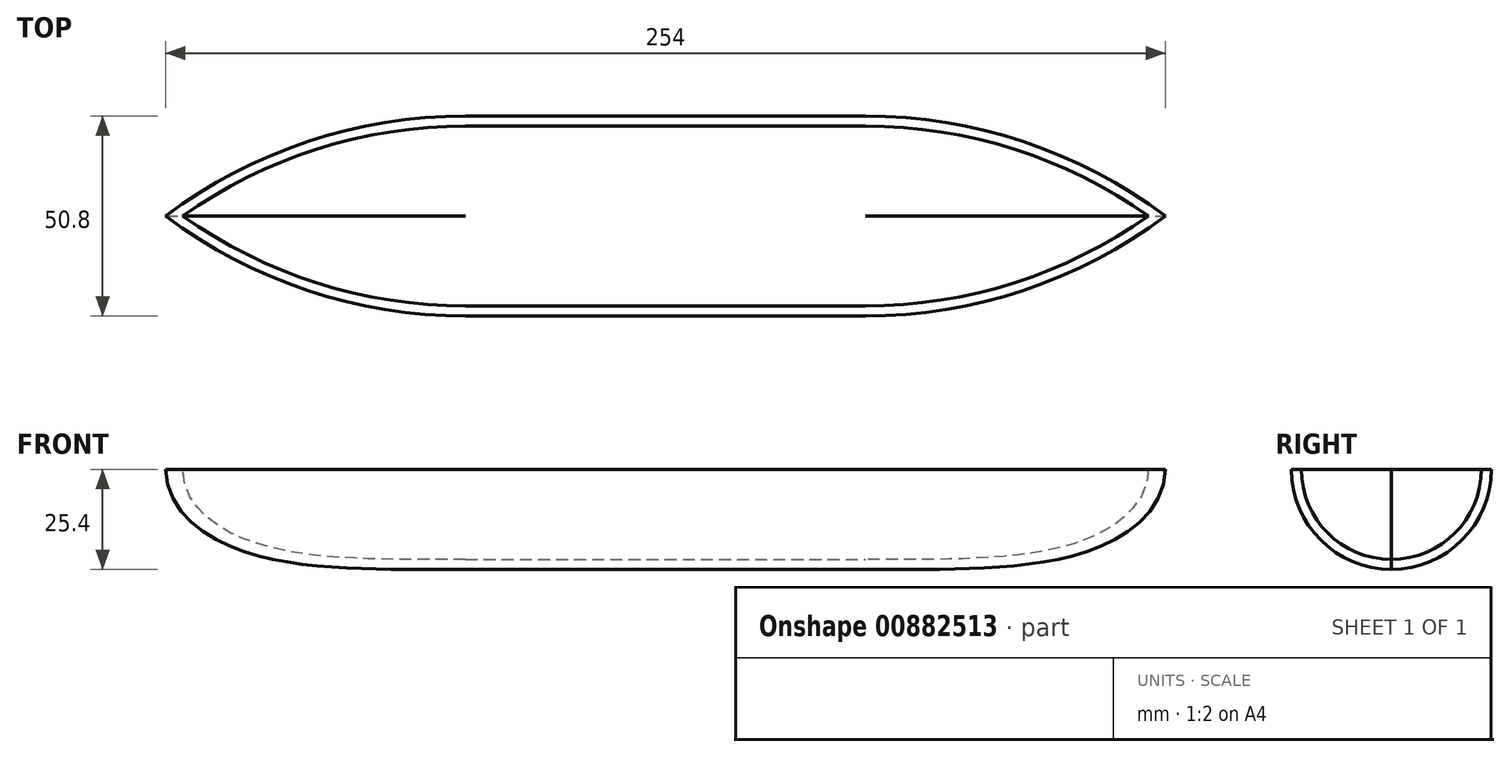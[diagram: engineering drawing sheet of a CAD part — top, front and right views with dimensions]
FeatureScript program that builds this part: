
annotation { "Feature Type Name" : "Feature", "Feature Type Description" : "" }
export const myFeature = defineFeature(function(context is Context, id is Id, definition is map)
    precondition{}
    {
        {
            var Q0;
            Q0=qCreatedBy(makeId("Top.planeOp"),FACE);
            var sketch = newSketch(context, id + "F0", { "sketchPlane" : qUnion([Q0])});
            skLineSegment(sketch, "E0.bottom", {"start": v(-127, 25.4) * mm, "end": v(127, 25.4) * mm});
            skLineSegment(sketch, "E0.top", {"start": v(-127, -25.4) * mm, "end": v(127, -25.4) * mm});
            skLineSegment(sketch, "E0.left", {"start": v(-127, 25.4) * mm, "end": v(-127, -25.4) * mm});
            skLineSegment(sketch, "E0.right", {"start": v(127, 25.4) * mm, "end": v(127, -25.4) * mm});
            skPoint(sketch, "E0.middle", {"position": v(0, 0) * mm});
            skSolve(sketch);
        }
        {
            var Q0;
            Q0=makeQuery(id+"F0.imprint","IMPRINT",FACE,{"disambiguationData":[TD([[makeQuery(id+"F0.imprint","IMPRINT",EDGE,{"derivedFrom":sQuery(id+"F0.wireOp",EDGE,"E0.bottom")}),-1.0]])]});
            extrude(context, id + "F1", {"entities" : qUnion([Q0]), "depth" : 25.4 * mm, "offsetDistance" : 25.4 * mm});
        }
        {
            var Q0;
            Q0=makeQuery(id+"F1.opExtrude","SWEPT_EDGE",EDGE,{"disambiguationData":[OSD([sQuery(id+"F0.wireOp",EDGE,"E0.top"),sQuery(id+"F0.wireOp",EDGE,"E0.right")])]});
            var Q1;
            Q1=makeQuery(id+"F1.opExtrude","SWEPT_EDGE",EDGE,{"disambiguationData":[OSD([sQuery(id+"F0.wireOp",EDGE,"E0.bottom"),sQuery(id+"F0.wireOp",EDGE,"E0.right")])]});
            var Q2;
            Q2=makeQuery(id+"F1.opExtrude","SWEPT_EDGE",EDGE,{"disambiguationData":[OSD([sQuery(id+"F0.wireOp",EDGE,"E0.top"),sQuery(id+"F0.wireOp",EDGE,"E0.left")])]});
            var Q3;
            Q3=makeQuery(id+"F1.opExtrude","SWEPT_EDGE",EDGE,{"disambiguationData":[OSD([sQuery(id+"F0.wireOp",EDGE,"E0.bottom"),sQuery(id+"F0.wireOp",EDGE,"E0.left")])]});
            chamfer(context, id + "F2", {"entities" : qUnion([Q0, Q1, Q2, Q3]), "width" : 25.4 * mm, "tangentPropagation" : true});
        }
        {
            var Q0;
            {var subQ0=sQuery(id+"F0.wireOp",EDGE,"E0.top");Q0=makeQuery(id+"F2.opChamfer","BLEND_EDGE",EDGE,{"blendedFrom":[makeQuery(id+"F1.opExtrude","SWEPT_EDGE",EDGE,{"disambiguationData":[OSD([subQ0,sQuery(id+"F0.wireOp",EDGE,"E0.right")])]}),makeQuery(id+"F1.opExtrude","SWEPT_FACE",FACE,{"disambiguationData":[OSD([subQ0])]})],"blendedInto":[makeQuery(id+"F1.opExtrude","SWEPT_FACE",FACE,{"disambiguationData":[OSD([subQ0])]})]});}
            var Q1;
            {var subQ0=sQuery(id+"F0.wireOp",EDGE,"E0.top");Q1=makeQuery(id+"F2.opChamfer","BLEND_EDGE",EDGE,{"blendedFrom":[makeQuery(id+"F1.opExtrude","SWEPT_EDGE",EDGE,{"disambiguationData":[OSD([subQ0,sQuery(id+"F0.wireOp",EDGE,"E0.left")])]}),makeQuery(id+"F1.opExtrude","SWEPT_FACE",FACE,{"disambiguationData":[OSD([subQ0])]})],"blendedInto":[makeQuery(id+"F1.opExtrude","SWEPT_FACE",FACE,{"disambiguationData":[OSD([subQ0])]})]});}
            var Q2;
            {var subQ0=sQuery(id+"F0.wireOp",EDGE,"E0.bottom");Q2=makeQuery(id+"F2.opChamfer","BLEND_EDGE",EDGE,{"blendedFrom":[makeQuery(id+"F1.opExtrude","SWEPT_EDGE",EDGE,{"disambiguationData":[OSD([subQ0,sQuery(id+"F0.wireOp",EDGE,"E0.right")])]}),makeQuery(id+"F1.opExtrude","SWEPT_FACE",FACE,{"disambiguationData":[OSD([subQ0])]})],"blendedInto":[makeQuery(id+"F1.opExtrude","SWEPT_FACE",FACE,{"disambiguationData":[OSD([subQ0])]})]});}
            var Q3;
            {var subQ0=sQuery(id+"F0.wireOp",EDGE,"E0.bottom");Q3=makeQuery(id+"F2.opChamfer","BLEND_EDGE",EDGE,{"blendedFrom":[makeQuery(id+"F1.opExtrude","SWEPT_EDGE",EDGE,{"disambiguationData":[OSD([subQ0,sQuery(id+"F0.wireOp",EDGE,"E0.left")])]}),makeQuery(id+"F1.opExtrude","SWEPT_FACE",FACE,{"disambiguationData":[OSD([subQ0])]})],"blendedInto":[makeQuery(id+"F1.opExtrude","SWEPT_FACE",FACE,{"disambiguationData":[OSD([subQ0])]})]});}
            fillet(context, id + "F3", {"entities" : qUnion([Q0, Q1, Q2, Q3]), "radius" : 127 * mm, "tangentPropagation" : true, "allowEdgeOverflow" : false});
        }
        {
            var Q0;
            {var subQ0=sQuery(id+"F0.wireOp",EDGE,"E0.left");var subQ1=sQuery(id+"F0.wireOp",EDGE,"E0.top");Q0=makeQuery(id+"F3.opFillet","BLEND_EDGE",EDGE,{"blendedFrom":[makeQuery(id+"F2.opChamfer","BLEND_EDGE",EDGE,{"blendedFrom":[makeQuery(id+"F1.opExtrude","SWEPT_EDGE",EDGE,{"disambiguationData":[OSD([subQ1,subQ0])]}),makeQuery(id+"F1.opExtrude","SWEPT_FACE",FACE,{"disambiguationData":[OSD([subQ1])]})],"blendedInto":[makeQuery(id+"F1.opExtrude","SWEPT_FACE",FACE,{"disambiguationData":[OSD([subQ1])]})]}),makeQuery(id+"F1.opExtrude","CAP_FACE",FACE,{"disambiguationData":[OSD([sQuery(id+"F0.wireOp",EDGE,"E0.bottom"),subQ1,subQ0,sQuery(id+"F0.wireOp",EDGE,"E0.right")])],"isStart":true})],"blendedInto":[makeQuery(id+"F1.opExtrude","CAP_FACE",FACE,{"disambiguationData":[OSD([sQuery(id+"F0.wireOp",EDGE,"E0.bottom"),subQ1,subQ0,sQuery(id+"F0.wireOp",EDGE,"E0.right")])],"isStart":true})]});}
            var Q1;
            Q1=makeQuery(id+"F1.opExtrude","CAP_EDGE",EDGE,{"disambiguationData":[OSD([sQuery(id+"F0.wireOp",EDGE,"E0.top")])],"isStart":true});
            var Q2;
            {var subQ0=sQuery(id+"F0.wireOp",EDGE,"E0.right");var subQ1=sQuery(id+"F0.wireOp",EDGE,"E0.top");Q2=makeQuery(id+"F3.opFillet","BLEND_EDGE",EDGE,{"blendedFrom":[makeQuery(id+"F2.opChamfer","BLEND_EDGE",EDGE,{"blendedFrom":[makeQuery(id+"F1.opExtrude","SWEPT_EDGE",EDGE,{"disambiguationData":[OSD([subQ1,subQ0])]}),makeQuery(id+"F1.opExtrude","SWEPT_FACE",FACE,{"disambiguationData":[OSD([subQ1])]})],"blendedInto":[makeQuery(id+"F1.opExtrude","SWEPT_FACE",FACE,{"disambiguationData":[OSD([subQ1])]})]}),makeQuery(id+"F1.opExtrude","CAP_FACE",FACE,{"disambiguationData":[OSD([sQuery(id+"F0.wireOp",EDGE,"E0.bottom"),subQ1,sQuery(id+"F0.wireOp",EDGE,"E0.left"),subQ0])],"isStart":true})],"blendedInto":[makeQuery(id+"F1.opExtrude","CAP_FACE",FACE,{"disambiguationData":[OSD([sQuery(id+"F0.wireOp",EDGE,"E0.bottom"),subQ1,sQuery(id+"F0.wireOp",EDGE,"E0.left"),subQ0])],"isStart":true})]});}
            var Q3;
            {var subQ0=sQuery(id+"F0.wireOp",EDGE,"E0.right");var subQ1=sQuery(id+"F0.wireOp",EDGE,"E0.bottom");Q3=makeQuery(id+"F3.opFillet","BLEND_EDGE",EDGE,{"blendedFrom":[makeQuery(id+"F2.opChamfer","BLEND_EDGE",EDGE,{"blendedFrom":[makeQuery(id+"F1.opExtrude","SWEPT_EDGE",EDGE,{"disambiguationData":[OSD([subQ1,subQ0])]}),makeQuery(id+"F1.opExtrude","SWEPT_FACE",FACE,{"disambiguationData":[OSD([subQ1])]})],"blendedInto":[makeQuery(id+"F1.opExtrude","SWEPT_FACE",FACE,{"disambiguationData":[OSD([subQ1])]})]}),makeQuery(id+"F1.opExtrude","CAP_FACE",FACE,{"disambiguationData":[OSD([subQ1,sQuery(id+"F0.wireOp",EDGE,"E0.top"),sQuery(id+"F0.wireOp",EDGE,"E0.left"),subQ0])],"isStart":true})],"blendedInto":[makeQuery(id+"F1.opExtrude","CAP_FACE",FACE,{"disambiguationData":[OSD([subQ1,sQuery(id+"F0.wireOp",EDGE,"E0.top"),sQuery(id+"F0.wireOp",EDGE,"E0.left"),subQ0])],"isStart":true})]});}
            var Q4;
            Q4=makeQuery(id+"F1.opExtrude","CAP_EDGE",EDGE,{"disambiguationData":[OSD([sQuery(id+"F0.wireOp",EDGE,"E0.bottom")])],"isStart":true});
            var Q5;
            {var subQ0=sQuery(id+"F0.wireOp",EDGE,"E0.left");var subQ1=sQuery(id+"F0.wireOp",EDGE,"E0.bottom");Q5=makeQuery(id+"F3.opFillet","BLEND_EDGE",EDGE,{"blendedFrom":[makeQuery(id+"F2.opChamfer","BLEND_EDGE",EDGE,{"blendedFrom":[makeQuery(id+"F1.opExtrude","SWEPT_EDGE",EDGE,{"disambiguationData":[OSD([subQ1,subQ0])]}),makeQuery(id+"F1.opExtrude","SWEPT_FACE",FACE,{"disambiguationData":[OSD([subQ1])]})],"blendedInto":[makeQuery(id+"F1.opExtrude","SWEPT_FACE",FACE,{"disambiguationData":[OSD([subQ1])]})]}),makeQuery(id+"F1.opExtrude","CAP_FACE",FACE,{"disambiguationData":[OSD([subQ1,sQuery(id+"F0.wireOp",EDGE,"E0.top"),subQ0,sQuery(id+"F0.wireOp",EDGE,"E0.right")])],"isStart":true})],"blendedInto":[makeQuery(id+"F1.opExtrude","CAP_FACE",FACE,{"disambiguationData":[OSD([subQ1,sQuery(id+"F0.wireOp",EDGE,"E0.top"),subQ0,sQuery(id+"F0.wireOp",EDGE,"E0.right")])],"isStart":true})]});}
            fillet(context, id + "F4", {"entities" : qUnion([Q0, Q1, Q2, Q3, Q4, Q5]), "radius" : 25.4 * mm, "tangentPropagation" : true, "allowEdgeOverflow" : false});
        }
        {
            var Q0;
            Q0=makeQuery(id+"F1.opExtrude","CAP_FACE",FACE,{"disambiguationData":[OSD([sQuery(id+"F0.wireOp",EDGE,"E0.bottom"),sQuery(id+"F0.wireOp",EDGE,"E0.top"),sQuery(id+"F0.wireOp",EDGE,"E0.left"),sQuery(id+"F0.wireOp",EDGE,"E0.right")])],"isStart":false});
            shell(context, id + "F5", {"entities" : qUnion([Q0]), "thickness" : 2.54 * mm});
        }
    });
